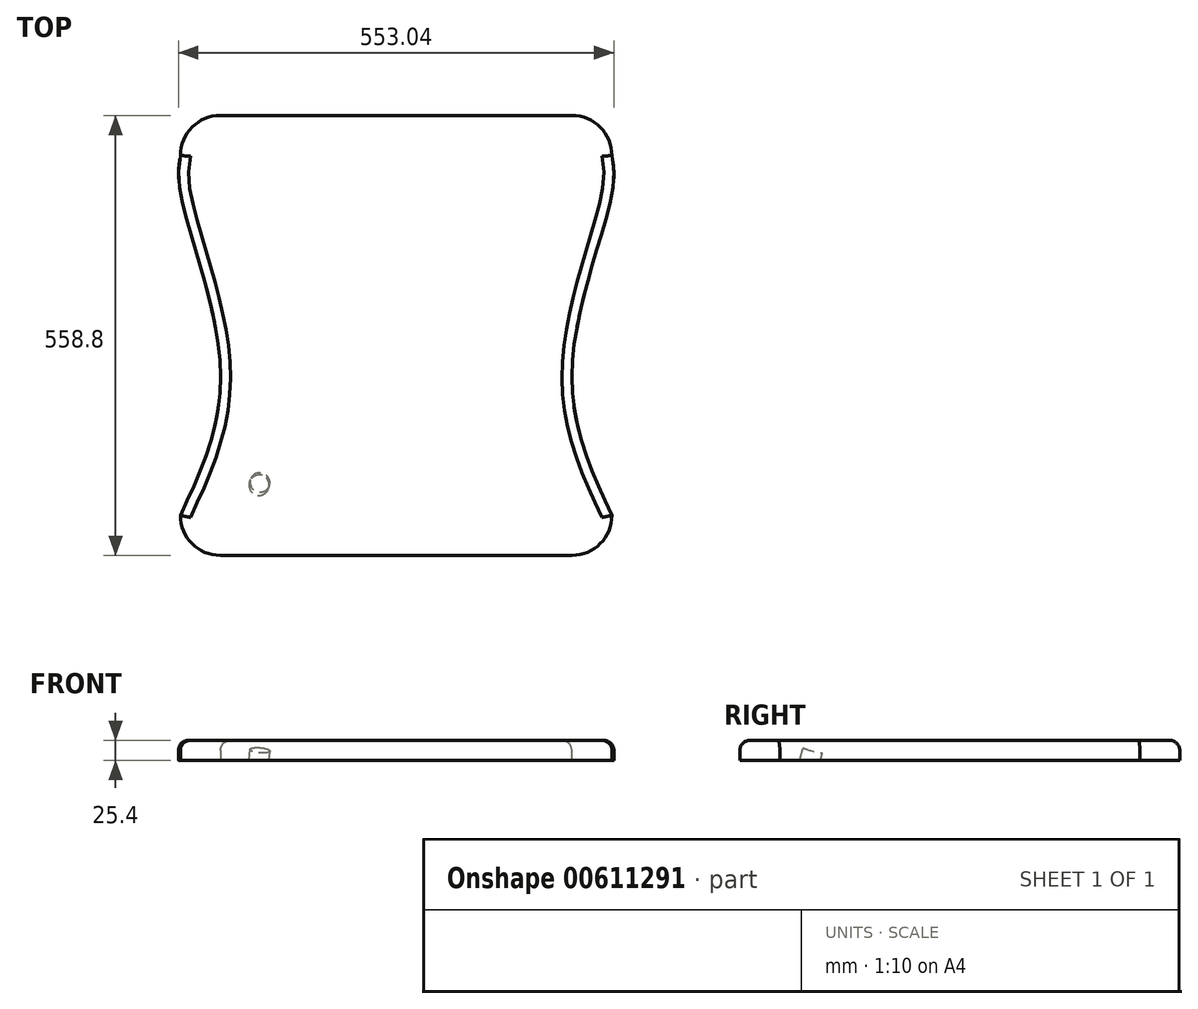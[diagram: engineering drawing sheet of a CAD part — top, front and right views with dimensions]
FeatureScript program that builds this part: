
annotation { "Feature Type Name" : "Feature", "Feature Type Description" : "" }
export const myFeature = defineFeature(function(context is Context, id is Id, definition is map)
    precondition{}
    {
        {
            var Q0;
            Q0=qCreatedBy(makeId("Top.planeOp"),FACE);
            var sketch = newSketch(context, id + "F0", { "sketchPlane" : qUnion([Q0])});
            skLineSegment(sketch, "E0.bottom", {"start": v(-235.8, 320.88) * mm, "end": v(210.82, 320.88) * mm});
            skLineSegment(sketch, "E0.top", {"start": v(-235.8, -237.92) * mm, "end": v(210.82, -237.92) * mm});
            skPoint(sketch, "E1.visualSharp", {"position": v(-286.6, 320.88) * mm});
            skArc(sketch, "E1.filletArc", {"start": v(-235.8, 320.88) * mm, "mid": v(-271.72, 306) * mm, "end": v(-286.6, 270.08) * mm});
            skPoint(sketch, "E2.visualSharp", {"position": v(261.62, 320.88) * mm});
            skArc(sketch, "E2.filletArc", {"start": v(261.62, 270.08) * mm, "mid": v(246.74, 306) * mm, "end": v(210.82, 320.88) * mm});
            skPoint(sketch, "E3.visualSharp", {"position": v(261.62, -237.92) * mm});
            skArc(sketch, "E3.filletArc", {"start": v(210.82, -237.92) * mm, "mid": v(246.74, -223.04) * mm, "end": v(261.62, -187.12) * mm});
            skPoint(sketch, "E4.visualSharp", {"position": v(-286.6, -237.92) * mm});
            skArc(sketch, "E4.filletArc", {"start": v(-286.6, -187.12) * mm, "mid": v(-271.72, -223.04) * mm, "end": v(-235.8, -237.92) * mm});
            skFitSpline(sketch, "E5", {"points": [v(-286.6, -187.12) * mm, v(-235.82, 0) * mm, v(-286.6, 221.74) * mm, v(-286.6, 270.08) * mm], "startDerivative": vector(208.52, 446.14) * mm, "endDerivative": vector(32.32, 199.73) * mm});
            skArc(sketch, "E6.MirrorCS", {"start": v(261.62, -187.12) * mm, "mid": v(246.74, -223.04) * mm, "end": v(210.82, -237.92) * mm});
            skArc(sketch, "E7.MirrorCS", {"start": v(210.82, 320.88) * mm, "mid": v(246.74, 306) * mm, "end": v(261.62, 270.08) * mm});
            skFitSpline(sketch, "E8.MirrorCS", {"points": [v(261.62, -187.12) * mm, v(210.84, 0) * mm, v(261.62, 221.74) * mm, v(261.62, 270.08) * mm], "startDerivative": vector(-208.52, 446.14) * mm, "endDerivative": vector(-32.32, 199.73) * mm});
            skPoint(sketch, "E9.end.orphan", {"position": v(-12.5, -237.92) * mm});
            skPoint(sketch, "E9.start.orphan", {"position": v(-12.5, 320.88) * mm});
            skSolve(sketch);
        }
        {
            var Q0;
            Q0=makeQuery(id+"F0.imprint","IMPRINT",FACE,{"disambiguationData":[TD([[makeQuery(id+"F0.imprint","IMPRINT",EDGE,{"derivedFrom":sQuery(id+"F0.wireOp",EDGE,"E0.bottom")}),-1.0]])]});
            extrude(context, id + "F1", {"entities" : qUnion([Q0]), "depth" : 25.4 * mm, "offsetDistance" : 25.4 * mm});
        }
        {
            var Q0;
            Q0=makeQuery(id+"F1.opExtrude","CAP_FACE",FACE,{"disambiguationData":[OSD([sQuery(id+"F0.wireOp",EDGE,"E0.bottom"),sQuery(id+"F0.wireOp",EDGE,"E0.top"),sQuery(id+"F0.wireOp",EDGE,"E1.filletArc"),sQuery(id+"F0.wireOp",EDGE,"E4.filletArc"),sQuery(id+"F0.wireOp",EDGE,"E5"),sQuery(id+"F0.wireOp",EDGE,"E6.MirrorCS"),sQuery(id+"F0.wireOp",EDGE,"E7.MirrorCS"),sQuery(id+"F0.wireOp",EDGE,"E8.MirrorCS")])],"isStart":false});
            fillet(context, id + "F2", {"entities" : qUnion([Q0]), "radius" : 12.7 * mm, "tangentPropagation" : true, "allowEdgeOverflow" : false});
        }
        {
            var Q0;
            {var subQ0=sQuery(id+"F0.wireOp",EDGE,"E0.top");Q0=makeQuery(id+"F2.opFillet","BLEND_EDGE",EDGE,{"blendedFrom":[makeQuery(id+"F1.opExtrude","CAP_EDGE",EDGE,{"disambiguationData":[OSD([subQ0])],"isStart":false}),makeQuery(id+"F1.opExtrude","CAP_FACE",FACE,{"disambiguationData":[OSD([sQuery(id+"F0.wireOp",EDGE,"E0.bottom"),subQ0,sQuery(id+"F0.wireOp",EDGE,"E1.filletArc"),sQuery(id+"F0.wireOp",EDGE,"E4.filletArc"),sQuery(id+"F0.wireOp",EDGE,"E5"),sQuery(id+"F0.wireOp",EDGE,"E6.MirrorCS"),sQuery(id+"F0.wireOp",EDGE,"E7.MirrorCS"),sQuery(id+"F0.wireOp",EDGE,"E8.MirrorCS")])],"isStart":false})],"blendedInto":[makeQuery(id+"F1.opExtrude","CAP_FACE",FACE,{"disambiguationData":[OSD([sQuery(id+"F0.wireOp",EDGE,"E0.bottom"),subQ0,sQuery(id+"F0.wireOp",EDGE,"E1.filletArc"),sQuery(id+"F0.wireOp",EDGE,"E4.filletArc"),sQuery(id+"F0.wireOp",EDGE,"E5"),sQuery(id+"F0.wireOp",EDGE,"E6.MirrorCS"),sQuery(id+"F0.wireOp",EDGE,"E7.MirrorCS"),sQuery(id+"F0.wireOp",EDGE,"E8.MirrorCS")])],"isStart":false})]});}
            cPlane(context, id + "F3", {"entities" : qUnion([Q0]), "cplaneType" : CPlaneType.LINE_ANGLE, "offset" : 25.4 * mm, "angle" : 75 * degree, "width" : 152.4 * mm, "height" : 152.4 * mm});
        }
        {
            var Q0;
            Q0=qCreatedBy(id+"F3.planeOp",FACE);
            var sketch = newSketch(context, id + "F4", { "sketchPlane" : qUnion([Q0])});
            skLineSegment(sketch, "E10.bottom", {"start": v(-233.32, -165.07) * mm, "end": v(-178.93, -165.07) * mm});
            skLineSegment(sketch, "E10.top", {"start": v(-233.32, -284.72) * mm, "end": v(-178.93, -284.72) * mm});
            skLineSegment(sketch, "E10.left", {"start": v(-233.32, -165.07) * mm, "end": v(-233.32, -284.72) * mm});
            skLineSegment(sketch, "E10.right", {"start": v(-178.93, -165.07) * mm, "end": v(-178.93, -284.72) * mm});
            skSolve(sketch);
        }
        {
            var Q0;
            Q0=sQuery(id+"F4.wireOp",EDGE,"E10.left");
            cPlane(context, id + "F5", {"entities" : qUnion([Q0]), "cplaneType" : CPlaneType.LINE_ANGLE, "offset" : 25.4 * mm, "angle" : 175 * degree, "width" : 152.4 * mm, "height" : 152.4 * mm});
        }
        {
            var Q0;
            Q0=qCreatedBy(id+"F5.planeOp",FACE);
            var sketch = newSketch(context, id + "F6", { "sketchPlane" : qUnion([Q0])});
            skCircle(sketch, "E11", {"center": v(-182.55, -143.63) * mm, "radius": 12.7 * mm});
            skSolve(sketch);
        }
        {
            var Q0;
            Q0 = qSketchRegion(id + "F6", true);
            extrude(context, id + "F7", {"entities" : qUnion([Q0]), "operationType" : NewBodyOperationType.REMOVE, "endBound" : BoundingType.SYMMETRIC, "oppositeDirection" : true, "depth" : 25.4 * mm, "offsetDistance" : 25.4 * mm});
        }
    });
